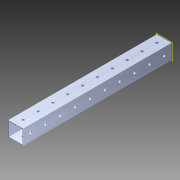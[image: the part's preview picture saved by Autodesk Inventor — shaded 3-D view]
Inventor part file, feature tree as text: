
AUTODESK INVENTOR PART (.ipt)
format: ipt  version: 2014 (Build 180170000, 170)  size: 1,159,168 bytes
history: native  units: in
note: dims shown in document units (in); Inventor stores cm internally (conversion verified against a paired STEP export)
features: pattern_circular x1, other x1, plane x1, extrude x1, imported_body x1, sketch x1
ambient origin geometry x8: Origin, YZ Plane, XZ Plane, XY Plane, X Axis, Y Axis, Z Axis, Center Point
bodies: Body1 (feature_tree)
feature tree (6):
  pattern_circular  "CirPattern2"
  other  "217-3426-STEP1"
  plane  "Work Plane1"
  extrude  "Extrusion1"  Depth=3937.0079in TaperAngle=0.0deg
  imported_body  "Base1"
  sketch  "Sketch1"  dims[d0=-10.0in d1=3937.0079in d2=0.0in]
